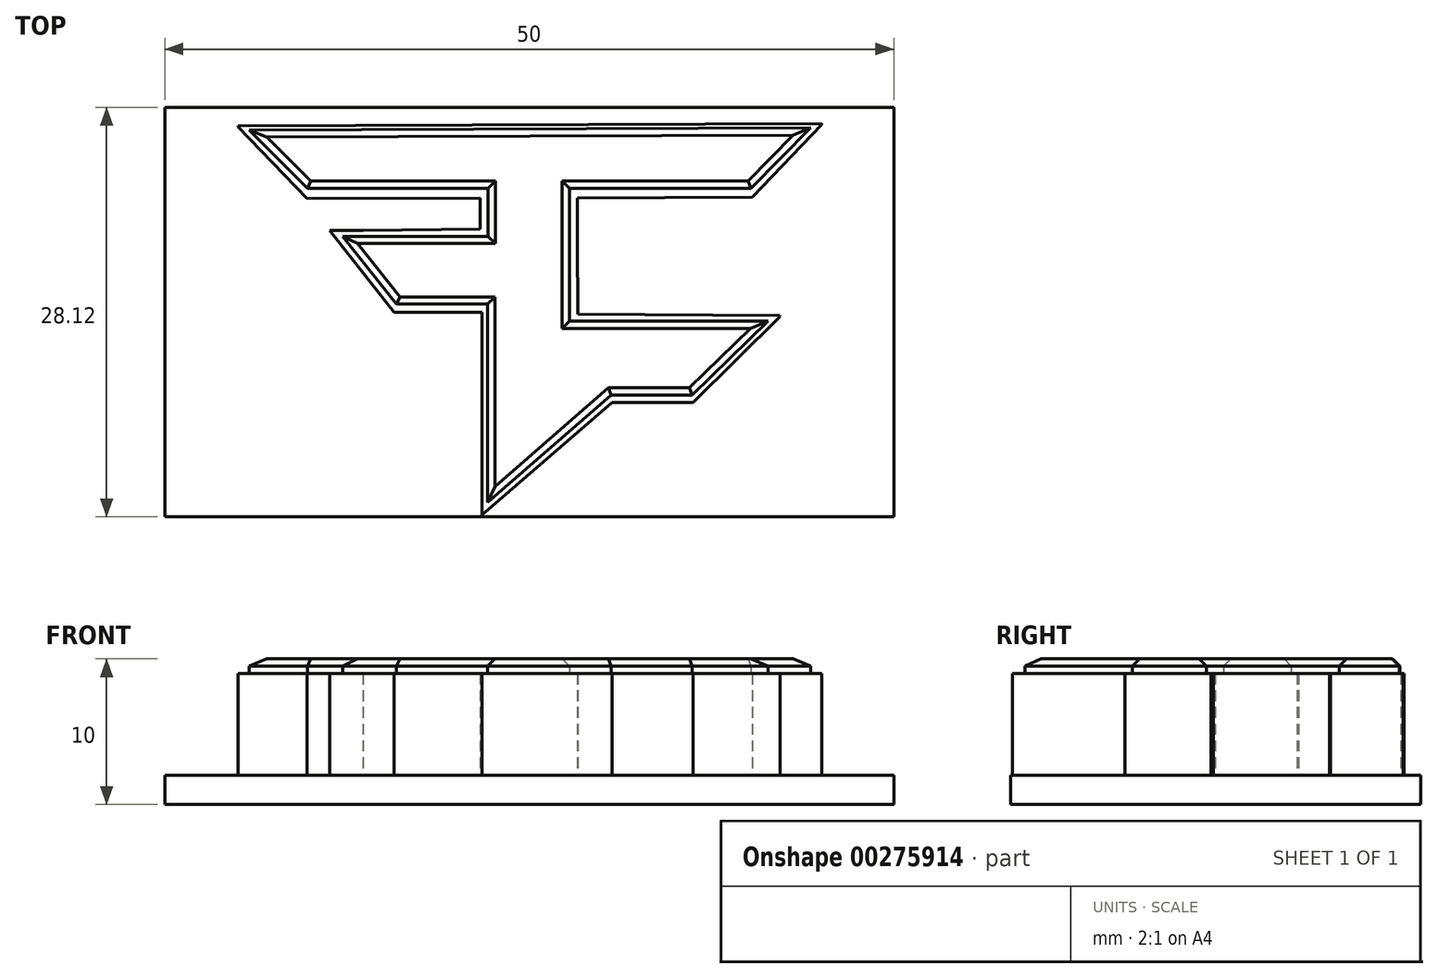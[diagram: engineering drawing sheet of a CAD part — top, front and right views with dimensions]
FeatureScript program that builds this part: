
annotation { "Feature Type Name" : "Feature", "Feature Type Description" : "" }
export const myFeature = defineFeature(function(context is Context, id is Id, definition is map)
    precondition{}
    {
        {
            var Q0;
            Q0=qCreatedBy(makeId("Top.planeOp"),FACE);
            var sketch = newSketch(context, id + "F0", { "sketchPlane" : qUnion([Q0])});
            skLineSegment(sketch, "E0", {"start": v(5.1, 26.83) * mm, "end": v(45.06, 27) * mm});
            skLineSegment(sketch, "E1", {"start": v(45.06, 27) * mm, "end": v(45.06, 26.93) * mm});
            skLineSegment(sketch, "E2", {"start": v(45.06, 26.93) * mm, "end": v(40.3, 21.95) * mm});
            skLineSegment(sketch, "E3", {"start": v(28.3, 18.97) * mm, "end": v(28.3, 13.92) * mm});
            skLineSegment(sketch, "E4", {"start": v(28.3, 13.92) * mm, "end": v(42.17, 13.81) * mm});
            skLineSegment(sketch, "E5", {"start": v(42.17, 13.81) * mm, "end": v(42.2, 13.76) * mm});
            skLineSegment(sketch, "E6", {"start": v(42.2, 13.76) * mm, "end": v(36.24, 7.84) * mm});
            skLineSegment(sketch, "E7", {"start": v(36.24, 7.84) * mm, "end": v(30.66, 7.84) * mm});
            skLineSegment(sketch, "E8", {"start": v(30.66, 7.84) * mm, "end": v(21.73, 0.12) * mm});
            skLineSegment(sketch, "E9", {"start": v(21.73, 0.12) * mm, "end": v(21.73, 13.64) * mm});
            skLineSegment(sketch, "E10", {"start": v(15.7, 14.05) * mm, "end": v(11.3, 19.66) * mm});
            skLineSegment(sketch, "E11", {"start": v(11.3, 19.66) * mm, "end": v(13.6, 19.66) * mm});
            skLineSegment(sketch, "E12", {"start": v(9.75, 21.85) * mm, "end": v(5.03, 26.78) * mm});
            skLineSegment(sketch, "E13", {"start": v(5.03, 26.78) * mm, "end": v(5.03, 26.83) * mm});
            skLineSegment(sketch, "E14", {"start": v(5.03, 26.83) * mm, "end": v(5.1, 26.83) * mm});
            skLineSegment(sketch, "E15", {"start": v(13.6, 19.66) * mm, "end": v(21.62, 19.74) * mm});
            skLineSegment(sketch, "E16", {"start": v(21.62, 19.74) * mm, "end": v(21.62, 21.9) * mm});
            skLineSegment(sketch, "E17", {"start": v(21.62, 21.9) * mm, "end": v(9.75, 21.85) * mm});
            skLineSegment(sketch, "E18", {"start": v(28.3, 18.97) * mm, "end": v(28.3, 21.87) * mm});
            skLineSegment(sketch, "E19", {"start": v(28.3, 21.87) * mm, "end": v(40.3, 21.95) * mm});
            skLineSegment(sketch, "E20", {"start": v(15.7, 14.05) * mm, "end": v(21.73, 14.05) * mm});
            skLineSegment(sketch, "E21", {"start": v(21.73, 14.05) * mm, "end": v(21.73, 13.64) * mm});
            skSolve(sketch);
        }
        {
            var Q0;
            Q0=makeQuery(id+"F0.imprint","IMPRINT",FACE,{"disambiguationData":[TD([[makeQuery(id+"F0.imprint","IMPRINT",EDGE,{"derivedFrom":sQuery(id+"F0.wireOp",EDGE,"E0")}),-1.0]])]});
            extrude(context, id + "F1", {"entities" : qUnion([Q0]), "depth" : 9 * mm});
        }
        {
            var Q0;
            Q0=qCreatedBy(makeId("Top.planeOp"),FACE);
            var sketch = newSketch(context, id + "F2", { "sketchPlane" : qUnion([Q0])});
            skLineSegment(sketch, "E22", {"start": v(5.78, 26.57) * mm, "end": v(44.3, 26.7) * mm});
            skLineSegment(sketch, "E23", {"start": v(44.3, 26.7) * mm, "end": v(40.2, 22.56) * mm});
            skLineSegment(sketch, "E24", {"start": v(40.2, 22.56) * mm, "end": v(27.75, 22.56) * mm});
            skLineSegment(sketch, "E25", {"start": v(27.75, 22.56) * mm, "end": v(27.75, 13.44) * mm});
            skLineSegment(sketch, "E26", {"start": v(27.75, 13.44) * mm, "end": v(41.38, 13.44) * mm});
            skLineSegment(sketch, "E27", {"start": v(41.38, 13.44) * mm, "end": v(36.17, 8.36) * mm});
            skLineSegment(sketch, "E28", {"start": v(36.17, 8.36) * mm, "end": v(30.6, 8.36) * mm});
            skLineSegment(sketch, "E29", {"start": v(30.6, 8.36) * mm, "end": v(22.14, 1) * mm});
            skLineSegment(sketch, "E30", {"start": v(22.14, 1) * mm, "end": v(22.14, 14.6) * mm});
            skLineSegment(sketch, "E31", {"start": v(22.14, 14.6) * mm, "end": v(15.87, 14.6) * mm});
            skLineSegment(sketch, "E32", {"start": v(15.87, 14.6) * mm, "end": v(12.18, 19.26) * mm});
            skLineSegment(sketch, "E33", {"start": v(12.18, 19.26) * mm, "end": v(22.17, 19.26) * mm});
            skLineSegment(sketch, "E34", {"start": v(22.17, 19.26) * mm, "end": v(22.17, 22.56) * mm});
            skLineSegment(sketch, "E35", {"start": v(22.17, 22.56) * mm, "end": v(9.78, 22.56) * mm});
            skLineSegment(sketch, "E36", {"start": v(9.78, 22.56) * mm, "end": v(5.78, 26.57) * mm});
            skSolve(sketch);
        }
        {
            var Q0;
            Q0 = qSketchRegion(id + "F2", true);
            extrude(context, id + "F3", {"entities" : qUnion([Q0]), "operationType" : NewBodyOperationType.ADD, "depth" : 10 * mm});
        }
        {
            var Q0;
            Q0=makeQuery(id+"F3.opExtrude","CAP_FACE",FACE,{"disambiguationData":[OSD([sQuery(id+"F2.wireOp",EDGE,"E22"),sQuery(id+"F2.wireOp",EDGE,"E23"),sQuery(id+"F2.wireOp",EDGE,"E24"),sQuery(id+"F2.wireOp",EDGE,"E25"),sQuery(id+"F2.wireOp",EDGE,"E26"),sQuery(id+"F2.wireOp",EDGE,"E27"),sQuery(id+"F2.wireOp",EDGE,"E28"),sQuery(id+"F2.wireOp",EDGE,"E29"),sQuery(id+"F2.wireOp",EDGE,"E30"),sQuery(id+"F2.wireOp",EDGE,"E31"),sQuery(id+"F2.wireOp",EDGE,"E32"),sQuery(id+"F2.wireOp",EDGE,"E33"),sQuery(id+"F2.wireOp",EDGE,"E34"),sQuery(id+"F2.wireOp",EDGE,"E35"),sQuery(id+"F2.wireOp",EDGE,"E36")])],"isStart":false});
            chamfer(context, id + "F4", {"entities" : qUnion([Q0]), "width" : .5 * mm, "tangentPropagation" : true});
        }
        {
            var Q0;
            Q0=qCreatedBy(makeId("Top.planeOp"),FACE);
            var sketch = newSketch(context, id + "F5", { "sketchPlane" : qUnion([Q0])});
            skLineSegment(sketch, "E37.bottom", {"start": v(0, 28.13) * mm, "end": v(50, 28.13) * mm});
            skLineSegment(sketch, "E37.top", {"start": v(0, 0) * mm, "end": v(50, 0) * mm});
            skLineSegment(sketch, "E37.left", {"start": v(0, 28.13) * mm, "end": v(0, 0) * mm});
            skLineSegment(sketch, "E37.right", {"start": v(50, 28.13) * mm, "end": v(50, 0) * mm});
            skSolve(sketch);
        }
        {
            var Q0;
            Q0 = qSketchRegion(id + "F5", true);
            extrude(context, id + "F6", {"entities" : qUnion([Q0]), "operationType" : NewBodyOperationType.ADD, "depth" : 2 * mm});
        }
    });
